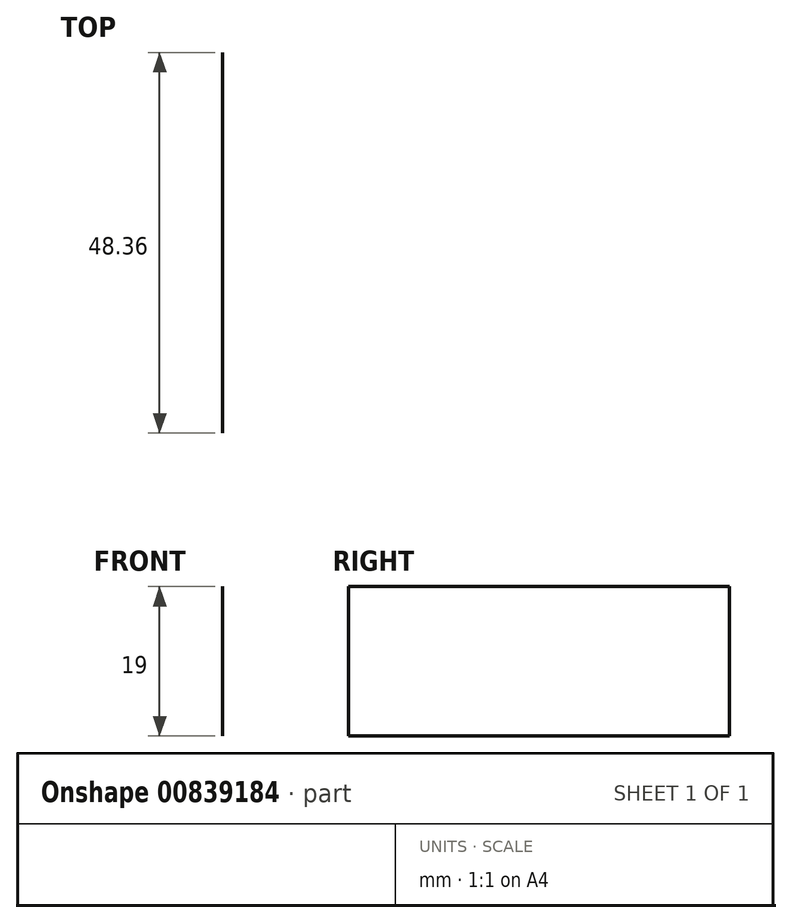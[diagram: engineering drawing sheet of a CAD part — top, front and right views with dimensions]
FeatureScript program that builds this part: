
annotation { "Feature Type Name" : "Feature", "Feature Type Description" : "" }
export const myFeature = defineFeature(function(context is Context, id is Id, definition is map)
    precondition{}
    {
        {
            var Q0;
            Q0=qCreatedBy(makeId("Top.planeOp"),FACE);
            var sketch = newSketch(context, id + "F0", { "sketchPlane" : qUnion([Q0])});
            skArc(sketch, "E0", {"start": v(0, -27.42) * mm, "mid": v(22.88, -3.24) * mm, "end": v(0, 20.94) * mm});
            skLineSegment(sketch, "E1", {"start": v(0, 20.94) * mm, "end": v(0, -27.42) * mm});
            skLineSegment(sketch, "E2", {"start": v(-10.05, -27.42) * mm, "end": v(-10.05, 20.94) * mm});
            skLineSegment(sketch, "E3", {"start": v(-10.05, 20.94) * mm, "end": v(0, 20.94) * mm});
            skLineSegment(sketch, "E4", {"start": v(-0.42, -27.42) * mm, "end": v(-10.05, -27.42) * mm});
            skArc(sketch, "E5", {"start": v(-10.05, 20.94) * mm, "mid": v(-29.1, -3.24) * mm, "end": v(-10.05, -27.42) * mm});
            skSolve(sketch);
        }
        {
            var Q0;
            Q0=sQuery(id+"F0.wireOp",EDGE,"E1");
            extrude(context, id + "F1", {"bodyType" : ToolBodyType.SURFACE, "surfaceEntities" : qUnion([Q0]), "depth" : 19 * mm, "offsetDistance" : 25.4 * mm});
        }
    });
